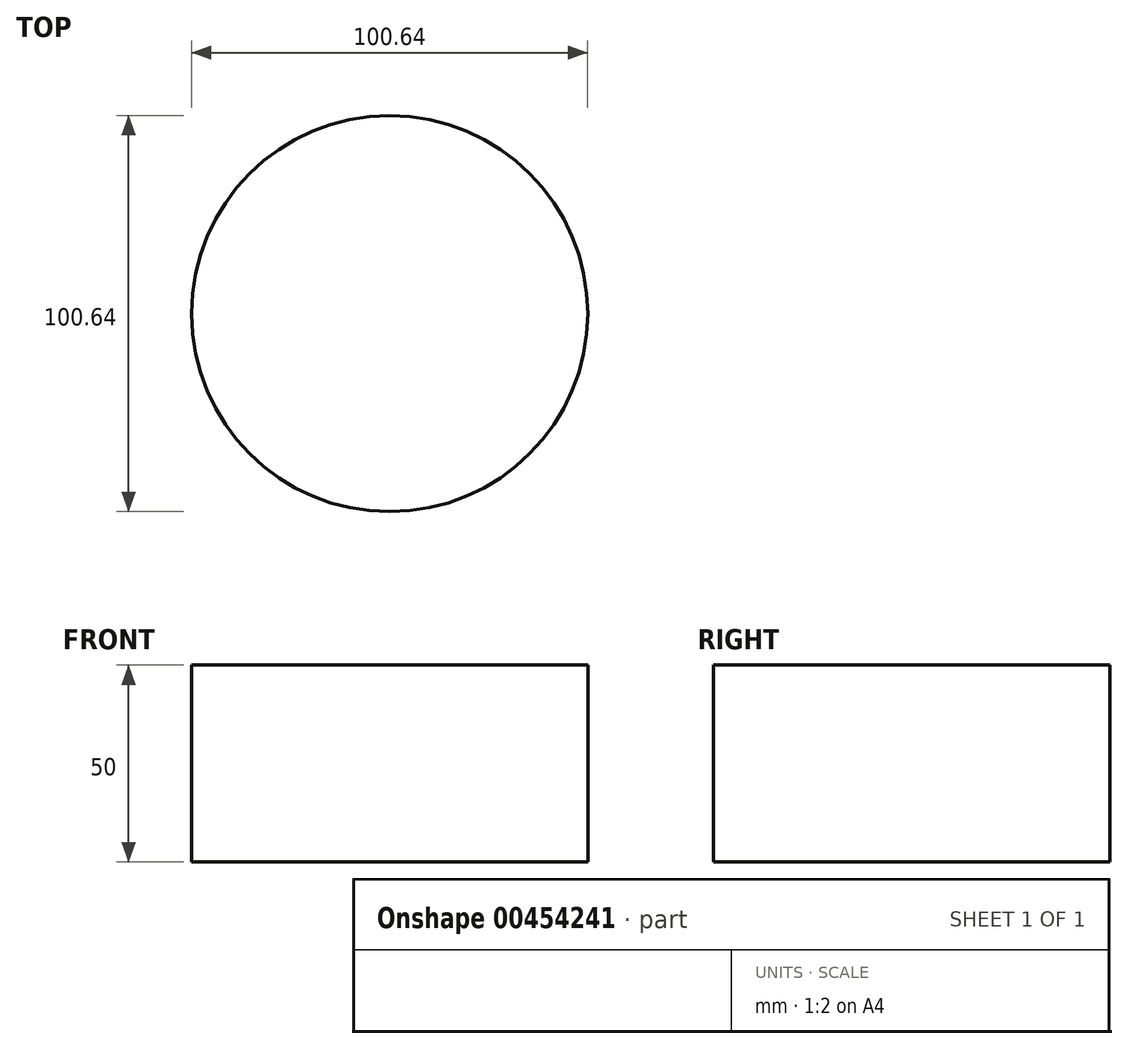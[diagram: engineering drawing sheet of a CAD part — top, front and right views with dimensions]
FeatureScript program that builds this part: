
annotation { "Feature Type Name" : "Feature", "Feature Type Description" : "" }
export const myFeature = defineFeature(function(context is Context, id is Id, definition is map)
    precondition{}
    {
        {
            var Q0;
            Q0=qCreatedBy(makeId("Top.planeOp"),FACE);
            var sketch = newSketch(context, id + "F0", { "sketchPlane" : qUnion([Q0])});
            skCircle(sketch, "E0", {"center": v(0, 0) * mm, "radius": 50.32 * mm});
            skSolve(sketch);
        }
        {
            var Q0;
            Q0 = qSketchRegion(id + "F0", true);
            extrude(context, id + "F1", {"entities" : qUnion([Q0]), "depth" : 50 * mm});
        }
    });
